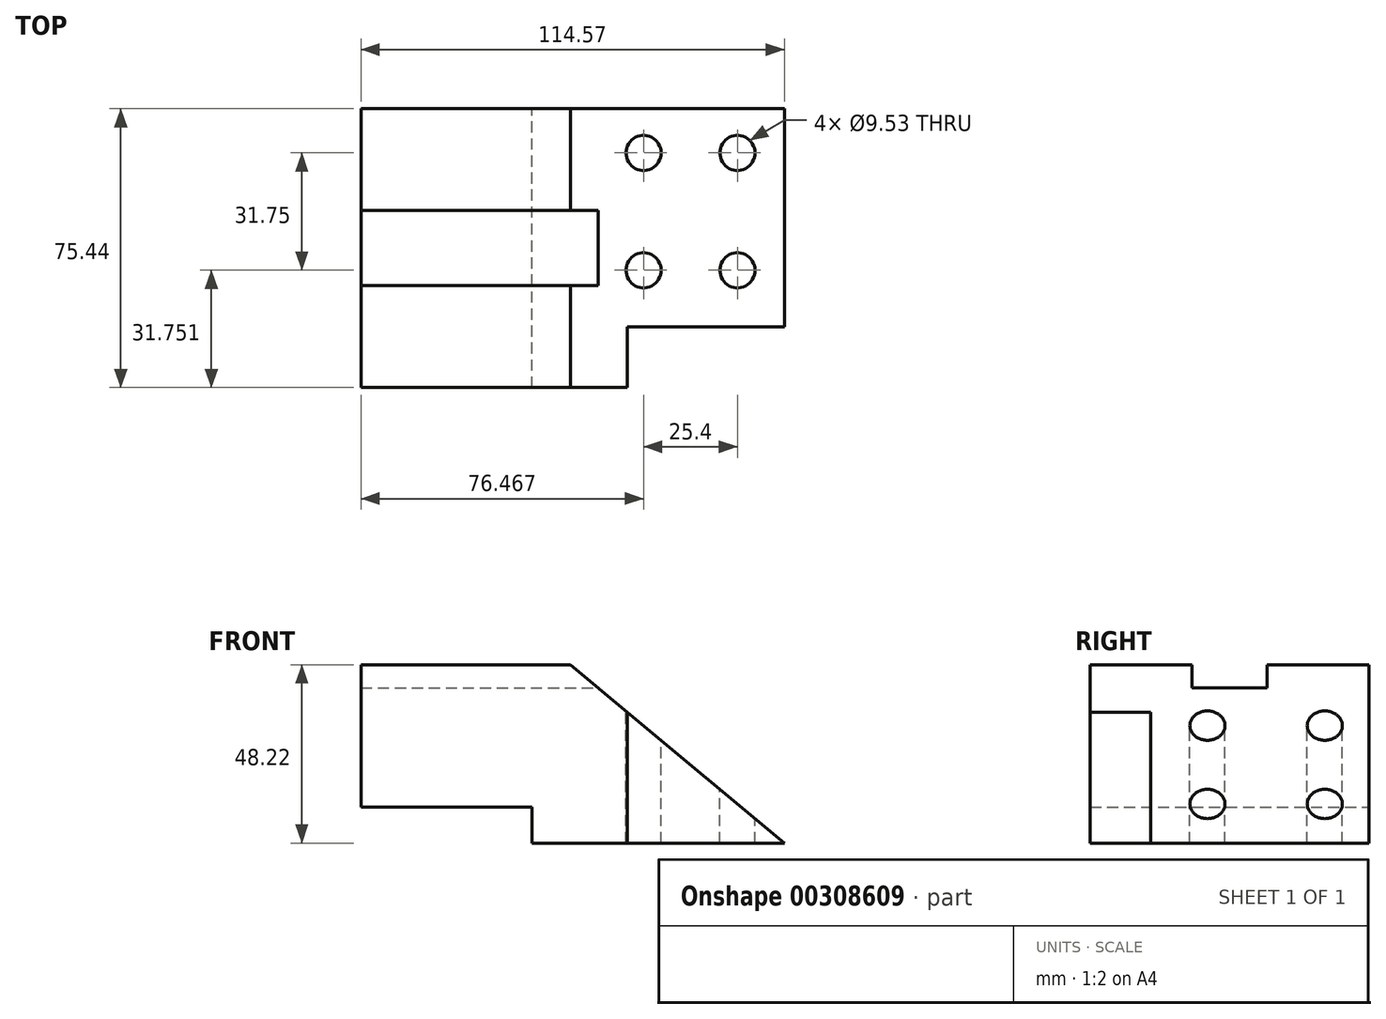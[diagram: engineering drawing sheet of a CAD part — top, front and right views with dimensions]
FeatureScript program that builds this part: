
annotation { "Feature Type Name" : "Feature", "Feature Type Description" : "" }
export const myFeature = defineFeature(function(context is Context, id is Id, definition is map)
    precondition{}
    {
        {
            var Q0;
            Q0=qCreatedBy(makeId("Front.planeOp"),FACE);
            var sketch = newSketch(context, id + "F0", { "sketchPlane" : qUnion([Q0])});
            skLineSegment(sketch, "E0", {"start": v(57.8, 0) * mm, "end": v(0, 48.22) * mm});
            skLineSegment(sketch, "E1", {"start": v(0, 48.22) * mm, "end": v(-56.76, 48.22) * mm});
            skLineSegment(sketch, "E2", {"start": v(-56.76, 48.22) * mm, "end": v(-56.76, 9.72) * mm});
            skLineSegment(sketch, "E3", {"start": v(-56.76, 9.72) * mm, "end": v(-10.51, 9.72) * mm});
            skLineSegment(sketch, "E4", {"start": v(-10.51, 9.72) * mm, "end": v(-10.51, 0) * mm});
            skLineSegment(sketch, "E5", {"start": v(-10.51, 0) * mm, "end": v(57.8, 0) * mm});
            skSolve(sketch);
        }
        {
            var Q0;
            Q0=makeQuery(id+"F0.imprint","IMPRINT",FACE,{"disambiguationData":[TD([[makeQuery(id+"F0.imprint","IMPRINT",EDGE,{"derivedFrom":sQuery(id+"F0.wireOp",EDGE,"E0")}),1.0]])]});
            extrude(context, id + "F1", {"entities" : qUnion([Q0]), "endBound" : BoundingType.SYMMETRIC, "depth" : 75.44 * mm});
        }
        {
            var Q0;
            Q0=makeQuery(id+"F1.opExtrude","SWEPT_FACE",FACE,{"disambiguationData":[OSD([sQuery(id+"F0.wireOp",EDGE,"E1")])]});
            var sketch = newSketch(context, id + "F2", { "sketchPlane" : qUnion([Q0])});
            skLineSegment(sketch, "E6.bottom", {"start": v(57.8, -37.72) * mm, "end": v(15.36, -37.72) * mm});
            skLineSegment(sketch, "E6.top", {"start": v(57.8, -21.33) * mm, "end": v(15.36, -21.33) * mm});
            skLineSegment(sketch, "E6.left", {"start": v(57.8, -37.72) * mm, "end": v(57.8, -21.33) * mm});
            skLineSegment(sketch, "E6.right", {"start": v(15.36, -37.72) * mm, "end": v(15.36, -21.33) * mm});
            skSolve(sketch);
        }
        {
            var Q0;
            Q0=makeQuery(id+"F2.imprint","IMPRINT",FACE,{"disambiguationData":[TD([[makeQuery(id+"F2.imprint","IMPRINT",EDGE,{"derivedFrom":sQuery(id+"F2.wireOp",EDGE,"E6.bottom")}),-1.0]])]});
            extrude(context, id + "F3", {"entities" : qUnion([Q0]), "operationType" : NewBodyOperationType.REMOVE, "endBound" : BoundingType.THROUGH_ALL, "oppositeDirection" : true, "depth" : 25.4 * mm});
        }
        {
            var Q0;
            Q0=qCreatedBy(makeId("Right.planeOp"),FACE);
            var sketch = newSketch(context, id + "F4", { "sketchPlane" : qUnion([Q0])});
            skLineSegment(sketch, "E7", {"start": v(0, 0) * mm, "end": v(0, 48.22) * mm, "construction": true});
            skLineSegment(sketch, "E8", {"start": v(-10.16, 42.04) * mm, "end": v(-10.16, 48.22) * mm});
            skLineSegment(sketch, "E9.0.MirrorCS", {"start": v(10.16, 42.04) * mm, "end": v(10.16, 48.22) * mm});
            skLineSegment(sketch, "E10", {"start": v(-10.16, 48.22) * mm, "end": v(10.16, 48.22) * mm});
            skLineSegment(sketch, "E11", {"start": v(-10.16, 42.04) * mm, "end": v(10.16, 42.04) * mm});
            skSolve(sketch);
        }
        {
            var Q0;
            Q0=makeQuery(id+"F4.imprint","IMPRINT",FACE,{"disambiguationData":[TD([[makeQuery(id+"F4.imprint","IMPRINT",EDGE,{"derivedFrom":sQuery(id+"F4.wireOp",EDGE,"E8")}),-1.0]])]});
            extrude(context, id + "F5", {"entities" : qUnion([Q0]), "operationType" : NewBodyOperationType.REMOVE, "endBound" : BoundingType.THROUGH_ALL, "oppositeDirection" : true, "depth" : 25.4 * mm, "hasSecondDirection" : true, "secondDirectionBound" : SecondDirectionBoundingType.THROUGH_ALL, "secondDirectionOppositeDirection" : false, "secondDirectionDepth" : 25.4 * mm});
        }
        {
            var Q0;
            Q0=makeQuery(id+"F1.opExtrude","SWEPT_FACE",FACE,{"disambiguationData":[OSD([sQuery(id+"F0.wireOp",EDGE,"E1")])]});
            var sketch = newSketch(context, id + "F6", { "sketchPlane" : qUnion([Q0])});
            skCircle(sketch, "E12", {"center": v(19.7, -5.97) * mm, "radius": 4.76 * mm});
            skCircle(sketch, "E13", {"center": v(45.1, 25.78) * mm, "radius": 4.76 * mm});
            skCircle(sketch, "E14", {"center": v(19.7, 25.78) * mm, "radius": 4.76 * mm});
            skCircle(sketch, "E15", {"center": v(45.1, -5.97) * mm, "radius": 4.76 * mm});
            skSolve(sketch);
        }
        {
            var Q0;
            Q0=makeQuery(id+"F6.imprint","IMPRINT",FACE,{"disambiguationData":[TD([[makeQuery(id+"F6.imprint","IMPRINT",EDGE,{"derivedFrom":sQuery(id+"F6.wireOp",EDGE,"E13")}),1.0]])]});
            var Q1;
            Q1=makeQuery(id+"F6.imprint","IMPRINT",FACE,{"disambiguationData":[TD([[makeQuery(id+"F6.imprint","IMPRINT",EDGE,{"derivedFrom":sQuery(id+"F6.wireOp",EDGE,"E14")}),1.0]])]});
            var Q2;
            Q2=makeQuery(id+"F6.imprint","IMPRINT",FACE,{"disambiguationData":[TD([[makeQuery(id+"F6.imprint","IMPRINT",EDGE,{"derivedFrom":sQuery(id+"F6.wireOp",EDGE,"E12")}),1.0]])]});
            var Q3;
            Q3=makeQuery(id+"F6.imprint","IMPRINT",FACE,{"disambiguationData":[TD([[makeQuery(id+"F6.imprint","IMPRINT",EDGE,{"derivedFrom":sQuery(id+"F6.wireOp",EDGE,"E15")}),1.0]])]});
            extrude(context, id + "F7", {"entities" : qUnion([Q0, Q1, Q2, Q3]), "operationType" : NewBodyOperationType.REMOVE, "endBound" : BoundingType.THROUGH_ALL, "oppositeDirection" : true, "depth" : 25.4 * mm});
        }
    });
